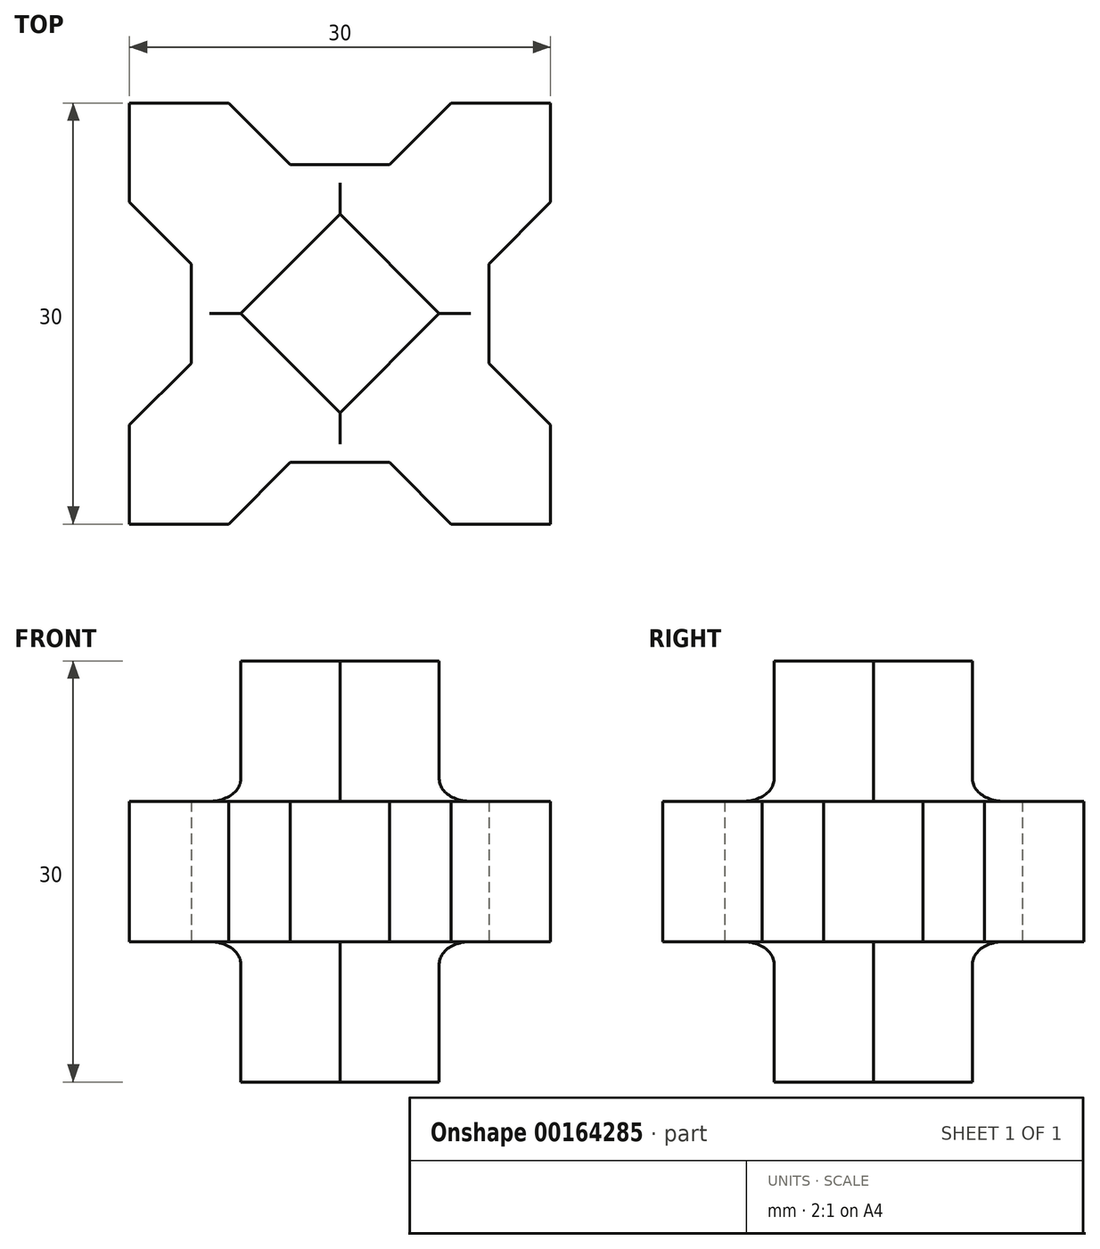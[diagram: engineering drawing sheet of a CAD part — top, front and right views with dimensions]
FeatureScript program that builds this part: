
annotation { "Feature Type Name" : "Feature", "Feature Type Description" : "" }
export const myFeature = defineFeature(function(context is Context, id is Id, definition is map)
    precondition{}
    {
        {
            assignVariable(context, id + "F0", {"name" : "D", "anyValue" : 30 * mm});
        }
        {
            var Q0;
            Q0=qCreatedBy(makeId("Top.planeOp"),FACE);
            var sketch = newSketch(context, id + "F1", { "sketchPlane" : qUnion([Q0])});
            skPoint(sketch, "E0.middle", {"position": v(0, 0) * mm});
            skLineSegment(sketch, "E1", {"start": v(-15, -15) * mm, "end": v(-7.93, -15) * mm});
            skLineSegment(sketch, "E2", {"start": v(-7.93, -15) * mm, "end": v(-3.54, -10.6) * mm});
            skLineSegment(sketch, "E3", {"start": v(-3.54, -10.6) * mm, "end": v(0, -10.6) * mm});
            skLineSegment(sketch, "E4", {"start": v(0, -7.07) * mm, "end": v(-3.54, -3.54) * mm});
            skLineSegment(sketch, "E5", {"start": v(-15, -15) * mm, "end": v(0, 0) * mm, "construction": true});
            skLineSegment(sketch, "E6.MirrorCS", {"start": v(-7.07, 0) * mm, "end": v(-3.54, -3.54) * mm});
            skLineSegment(sketch, "E7.MirrorCS", {"start": v(-10.6, -3.54) * mm, "end": v(-10.6, 0) * mm});
            skLineSegment(sketch, "E8.MirrorCS", {"start": v(-15, -15) * mm, "end": v(-15, -7.93) * mm});
            skLineSegment(sketch, "E9.MirrorCS", {"start": v(-15, -7.93) * mm, "end": v(-10.6, -3.54) * mm});
            skLineSegment(sketch, "E10.1.0", {"start": v(15, -7.93) * mm, "end": v(10.6, -3.54) * mm});
            skLineSegment(sketch, "E10.1.1", {"start": v(0, -7.07) * mm, "end": v(3.54, -3.54) * mm});
            skLineSegment(sketch, "E10.1.2", {"start": v(7.07, 0) * mm, "end": v(3.54, -3.54) * mm});
            skLineSegment(sketch, "E10.1.3", {"start": v(15, -15) * mm, "end": v(7.93, -15) * mm});
            skLineSegment(sketch, "E10.1.4", {"start": v(10.6, -3.54) * mm, "end": v(10.6, 0) * mm});
            skLineSegment(sketch, "E10.1.5", {"start": v(15, -15) * mm, "end": v(15, -7.93) * mm});
            skLineSegment(sketch, "E10.1.6", {"start": v(7.93, -15) * mm, "end": v(3.54, -10.6) * mm});
            skLineSegment(sketch, "E10.1.7", {"start": v(3.54, -10.6) * mm, "end": v(0, -10.6) * mm});
            skLineSegment(sketch, "E10.2.0", {"start": v(7.93, 15) * mm, "end": v(3.54, 10.6) * mm});
            skLineSegment(sketch, "E10.2.1", {"start": v(7.07, 0) * mm, "end": v(3.54, 3.54) * mm});
            skLineSegment(sketch, "E10.2.2", {"start": v(0, 7.07) * mm, "end": v(3.54, 3.54) * mm});
            skLineSegment(sketch, "E10.2.3", {"start": v(15, 15) * mm, "end": v(15, 7.93) * mm});
            skLineSegment(sketch, "E10.2.4", {"start": v(3.54, 10.6) * mm, "end": v(0, 10.6) * mm});
            skLineSegment(sketch, "E10.2.5", {"start": v(15, 15) * mm, "end": v(7.93, 15) * mm});
            skLineSegment(sketch, "E10.2.6", {"start": v(15, 7.93) * mm, "end": v(10.6, 3.54) * mm});
            skLineSegment(sketch, "E10.2.7", {"start": v(10.6, 3.54) * mm, "end": v(10.6, 0) * mm});
            skLineSegment(sketch, "E10.3.0", {"start": v(-15, 7.93) * mm, "end": v(-10.6, 3.54) * mm});
            skLineSegment(sketch, "E10.3.1", {"start": v(0, 7.07) * mm, "end": v(-3.54, 3.54) * mm});
            skLineSegment(sketch, "E10.3.2", {"start": v(-7.07, 0) * mm, "end": v(-3.54, 3.54) * mm});
            skLineSegment(sketch, "E10.3.3", {"start": v(-15, 15) * mm, "end": v(-7.93, 15) * mm});
            skLineSegment(sketch, "E10.3.4", {"start": v(-10.6, 3.54) * mm, "end": v(-10.6, 0) * mm});
            skLineSegment(sketch, "E10.3.5", {"start": v(-15, 15) * mm, "end": v(-15, 7.93) * mm});
            skLineSegment(sketch, "E10.3.6", {"start": v(-7.93, 15) * mm, "end": v(-3.54, 10.6) * mm});
            skLineSegment(sketch, "E10.3.7", {"start": v(-3.54, 10.6) * mm, "end": v(0, 10.6) * mm});
            skSolve(sketch);
        }
        {
            var Q0;
            Q0=makeQuery(id+"F1.imprint","IMPRINT",FACE,{"disambiguationData":[TD([[makeQuery(id+"F1.imprint","IMPRINT",EDGE,{"derivedFrom":sQuery(id+"F1.wireOp",EDGE,"E1")}),1.0]])]});
            var Q1;
            Q1=makeQuery(id+"F1.imprint","IMPRINT",FACE,{"disambiguationData":[TD([[makeQuery(id+"F1.imprint","IMPRINT",EDGE,{"derivedFrom":sQuery(id+"F1.wireOp",EDGE,"E4")}),-1.0]])]});
            extrude(context, id + "F2", {"entities" : qUnion([Q0, Q1]), "depth" : getVariable(context, 'D') / 3, "symmetric" : true});
        }
        {
            var Q0;
            Q0=makeQuery(id+"F1.imprint","IMPRINT",FACE,{"disambiguationData":[TD([[makeQuery(id+"F1.imprint","IMPRINT",EDGE,{"derivedFrom":sQuery(id+"F1.wireOp",EDGE,"E4")}),-1.0]])]});
            extrude(context, id + "F3", {"entities" : qUnion([Q0]), "operationType" : NewBodyOperationType.ADD, "depth" : getVariable(context, 'D'), "symmetric" : true});
        }
        {
            var Q0;
            Q0=makeQuery(id+"F3.boolean.opBoolean","INTERSECT",EDGE,{"derivedFrom":[makeQuery(id+"F2.opExtrude","CAP_FACE",FACE,{"disambiguationData":[OSD([sQuery(id+"F1.wireOp",EDGE,"E1"),sQuery(id+"F1.wireOp",EDGE,"E2"),sQuery(id+"F1.wireOp",EDGE,"E3"),sQuery(id+"F1.wireOp",EDGE,"E7.MirrorCS"),sQuery(id+"F1.wireOp",EDGE,"E8.MirrorCS"),sQuery(id+"F1.wireOp",EDGE,"E9.MirrorCS"),sQuery(id+"F1.wireOp",EDGE,"E10.1.0"),sQuery(id+"F1.wireOp",EDGE,"E10.1.3"),sQuery(id+"F1.wireOp",EDGE,"E10.1.4"),sQuery(id+"F1.wireOp",EDGE,"E10.1.5"),sQuery(id+"F1.wireOp",EDGE,"E10.1.6"),sQuery(id+"F1.wireOp",EDGE,"E10.1.7"),sQuery(id+"F1.wireOp",EDGE,"E10.2.0"),sQuery(id+"F1.wireOp",EDGE,"E10.2.3"),sQuery(id+"F1.wireOp",EDGE,"E10.2.4"),sQuery(id+"F1.wireOp",EDGE,"E10.2.5"),sQuery(id+"F1.wireOp",EDGE,"E10.2.6"),sQuery(id+"F1.wireOp",EDGE,"E10.2.7"),sQuery(id+"F1.wireOp",EDGE,"E10.3.0"),sQuery(id+"F1.wireOp",EDGE,"E10.3.3"),sQuery(id+"F1.wireOp",EDGE,"E10.3.4"),sQuery(id+"F1.wireOp",EDGE,"E10.3.5"),sQuery(id+"F1.wireOp",EDGE,"E10.3.6"),sQuery(id+"F1.wireOp",EDGE,"E10.3.7")])],"isStart":false}),makeQuery(id+"F3.opExtrude","SWEPT_FACE",FACE,{"disambiguationData":[OSD([sQuery(id+"F1.wireOp",EDGE,"E4"),sQuery(id+"F1.wireOp",EDGE,"E6.MirrorCS")])]})]});
            var Q1;
            Q1=makeQuery(id+"F3.boolean.opBoolean","INTERSECT",EDGE,{"derivedFrom":[makeQuery(id+"F2.opExtrude","CAP_FACE",FACE,{"disambiguationData":[OSD([sQuery(id+"F1.wireOp",EDGE,"E1"),sQuery(id+"F1.wireOp",EDGE,"E2"),sQuery(id+"F1.wireOp",EDGE,"E3"),sQuery(id+"F1.wireOp",EDGE,"E7.MirrorCS"),sQuery(id+"F1.wireOp",EDGE,"E8.MirrorCS"),sQuery(id+"F1.wireOp",EDGE,"E9.MirrorCS"),sQuery(id+"F1.wireOp",EDGE,"E10.1.0"),sQuery(id+"F1.wireOp",EDGE,"E10.1.3"),sQuery(id+"F1.wireOp",EDGE,"E10.1.4"),sQuery(id+"F1.wireOp",EDGE,"E10.1.5"),sQuery(id+"F1.wireOp",EDGE,"E10.1.6"),sQuery(id+"F1.wireOp",EDGE,"E10.1.7"),sQuery(id+"F1.wireOp",EDGE,"E10.2.0"),sQuery(id+"F1.wireOp",EDGE,"E10.2.3"),sQuery(id+"F1.wireOp",EDGE,"E10.2.4"),sQuery(id+"F1.wireOp",EDGE,"E10.2.5"),sQuery(id+"F1.wireOp",EDGE,"E10.2.6"),sQuery(id+"F1.wireOp",EDGE,"E10.2.7"),sQuery(id+"F1.wireOp",EDGE,"E10.3.0"),sQuery(id+"F1.wireOp",EDGE,"E10.3.3"),sQuery(id+"F1.wireOp",EDGE,"E10.3.4"),sQuery(id+"F1.wireOp",EDGE,"E10.3.5"),sQuery(id+"F1.wireOp",EDGE,"E10.3.6"),sQuery(id+"F1.wireOp",EDGE,"E10.3.7")])],"isStart":false}),makeQuery(id+"F3.opExtrude","SWEPT_FACE",FACE,{"disambiguationData":[OSD([sQuery(id+"F1.wireOp",EDGE,"E10.1.1"),sQuery(id+"F1.wireOp",EDGE,"E10.1.2")])]})]});
            var Q2;
            Q2=makeQuery(id+"F3.boolean.opBoolean","INTERSECT",EDGE,{"derivedFrom":[makeQuery(id+"F2.opExtrude","CAP_FACE",FACE,{"disambiguationData":[OSD([sQuery(id+"F1.wireOp",EDGE,"E1"),sQuery(id+"F1.wireOp",EDGE,"E2"),sQuery(id+"F1.wireOp",EDGE,"E3"),sQuery(id+"F1.wireOp",EDGE,"E7.MirrorCS"),sQuery(id+"F1.wireOp",EDGE,"E8.MirrorCS"),sQuery(id+"F1.wireOp",EDGE,"E9.MirrorCS"),sQuery(id+"F1.wireOp",EDGE,"E10.1.0"),sQuery(id+"F1.wireOp",EDGE,"E10.1.3"),sQuery(id+"F1.wireOp",EDGE,"E10.1.4"),sQuery(id+"F1.wireOp",EDGE,"E10.1.5"),sQuery(id+"F1.wireOp",EDGE,"E10.1.6"),sQuery(id+"F1.wireOp",EDGE,"E10.1.7"),sQuery(id+"F1.wireOp",EDGE,"E10.2.0"),sQuery(id+"F1.wireOp",EDGE,"E10.2.3"),sQuery(id+"F1.wireOp",EDGE,"E10.2.4"),sQuery(id+"F1.wireOp",EDGE,"E10.2.5"),sQuery(id+"F1.wireOp",EDGE,"E10.2.6"),sQuery(id+"F1.wireOp",EDGE,"E10.2.7"),sQuery(id+"F1.wireOp",EDGE,"E10.3.0"),sQuery(id+"F1.wireOp",EDGE,"E10.3.3"),sQuery(id+"F1.wireOp",EDGE,"E10.3.4"),sQuery(id+"F1.wireOp",EDGE,"E10.3.5"),sQuery(id+"F1.wireOp",EDGE,"E10.3.6"),sQuery(id+"F1.wireOp",EDGE,"E10.3.7")])],"isStart":false}),makeQuery(id+"F3.opExtrude","SWEPT_FACE",FACE,{"disambiguationData":[OSD([sQuery(id+"F1.wireOp",EDGE,"E10.2.1"),sQuery(id+"F1.wireOp",EDGE,"E10.2.2")])]})]});
            var Q3;
            Q3=makeQuery(id+"F3.boolean.opBoolean","INTERSECT",EDGE,{"derivedFrom":[makeQuery(id+"F2.opExtrude","CAP_FACE",FACE,{"disambiguationData":[OSD([sQuery(id+"F1.wireOp",EDGE,"E1"),sQuery(id+"F1.wireOp",EDGE,"E2"),sQuery(id+"F1.wireOp",EDGE,"E3"),sQuery(id+"F1.wireOp",EDGE,"E7.MirrorCS"),sQuery(id+"F1.wireOp",EDGE,"E8.MirrorCS"),sQuery(id+"F1.wireOp",EDGE,"E9.MirrorCS"),sQuery(id+"F1.wireOp",EDGE,"E10.1.0"),sQuery(id+"F1.wireOp",EDGE,"E10.1.3"),sQuery(id+"F1.wireOp",EDGE,"E10.1.4"),sQuery(id+"F1.wireOp",EDGE,"E10.1.5"),sQuery(id+"F1.wireOp",EDGE,"E10.1.6"),sQuery(id+"F1.wireOp",EDGE,"E10.1.7"),sQuery(id+"F1.wireOp",EDGE,"E10.2.0"),sQuery(id+"F1.wireOp",EDGE,"E10.2.3"),sQuery(id+"F1.wireOp",EDGE,"E10.2.4"),sQuery(id+"F1.wireOp",EDGE,"E10.2.5"),sQuery(id+"F1.wireOp",EDGE,"E10.2.6"),sQuery(id+"F1.wireOp",EDGE,"E10.2.7"),sQuery(id+"F1.wireOp",EDGE,"E10.3.0"),sQuery(id+"F1.wireOp",EDGE,"E10.3.3"),sQuery(id+"F1.wireOp",EDGE,"E10.3.4"),sQuery(id+"F1.wireOp",EDGE,"E10.3.5"),sQuery(id+"F1.wireOp",EDGE,"E10.3.6"),sQuery(id+"F1.wireOp",EDGE,"E10.3.7")])],"isStart":false}),makeQuery(id+"F3.opExtrude","SWEPT_FACE",FACE,{"disambiguationData":[OSD([sQuery(id+"F1.wireOp",EDGE,"E10.3.1"),sQuery(id+"F1.wireOp",EDGE,"E10.3.2")])]})]});
            var Q4;
            Q4=makeQuery(id+"F3.boolean.opBoolean","INTERSECT",EDGE,{"derivedFrom":[makeQuery(id+"F2.opExtrude","CAP_FACE",FACE,{"disambiguationData":[OSD([sQuery(id+"F1.wireOp",EDGE,"E1"),sQuery(id+"F1.wireOp",EDGE,"E2"),sQuery(id+"F1.wireOp",EDGE,"E3"),sQuery(id+"F1.wireOp",EDGE,"E7.MirrorCS"),sQuery(id+"F1.wireOp",EDGE,"E8.MirrorCS"),sQuery(id+"F1.wireOp",EDGE,"E9.MirrorCS"),sQuery(id+"F1.wireOp",EDGE,"E10.1.0"),sQuery(id+"F1.wireOp",EDGE,"E10.1.3"),sQuery(id+"F1.wireOp",EDGE,"E10.1.4"),sQuery(id+"F1.wireOp",EDGE,"E10.1.5"),sQuery(id+"F1.wireOp",EDGE,"E10.1.6"),sQuery(id+"F1.wireOp",EDGE,"E10.1.7"),sQuery(id+"F1.wireOp",EDGE,"E10.2.0"),sQuery(id+"F1.wireOp",EDGE,"E10.2.3"),sQuery(id+"F1.wireOp",EDGE,"E10.2.4"),sQuery(id+"F1.wireOp",EDGE,"E10.2.5"),sQuery(id+"F1.wireOp",EDGE,"E10.2.6"),sQuery(id+"F1.wireOp",EDGE,"E10.2.7"),sQuery(id+"F1.wireOp",EDGE,"E10.3.0"),sQuery(id+"F1.wireOp",EDGE,"E10.3.3"),sQuery(id+"F1.wireOp",EDGE,"E10.3.4"),sQuery(id+"F1.wireOp",EDGE,"E10.3.5"),sQuery(id+"F1.wireOp",EDGE,"E10.3.6"),sQuery(id+"F1.wireOp",EDGE,"E10.3.7")])],"isStart":true}),makeQuery(id+"F3.opExtrude","SWEPT_FACE",FACE,{"disambiguationData":[OSD([sQuery(id+"F1.wireOp",EDGE,"E10.3.1"),sQuery(id+"F1.wireOp",EDGE,"E10.3.2")])]})]});
            var Q5;
            Q5=makeQuery(id+"F3.boolean.opBoolean","INTERSECT",EDGE,{"derivedFrom":[makeQuery(id+"F2.opExtrude","CAP_FACE",FACE,{"disambiguationData":[OSD([sQuery(id+"F1.wireOp",EDGE,"E1"),sQuery(id+"F1.wireOp",EDGE,"E2"),sQuery(id+"F1.wireOp",EDGE,"E3"),sQuery(id+"F1.wireOp",EDGE,"E7.MirrorCS"),sQuery(id+"F1.wireOp",EDGE,"E8.MirrorCS"),sQuery(id+"F1.wireOp",EDGE,"E9.MirrorCS"),sQuery(id+"F1.wireOp",EDGE,"E10.1.0"),sQuery(id+"F1.wireOp",EDGE,"E10.1.3"),sQuery(id+"F1.wireOp",EDGE,"E10.1.4"),sQuery(id+"F1.wireOp",EDGE,"E10.1.5"),sQuery(id+"F1.wireOp",EDGE,"E10.1.6"),sQuery(id+"F1.wireOp",EDGE,"E10.1.7"),sQuery(id+"F1.wireOp",EDGE,"E10.2.0"),sQuery(id+"F1.wireOp",EDGE,"E10.2.3"),sQuery(id+"F1.wireOp",EDGE,"E10.2.4"),sQuery(id+"F1.wireOp",EDGE,"E10.2.5"),sQuery(id+"F1.wireOp",EDGE,"E10.2.6"),sQuery(id+"F1.wireOp",EDGE,"E10.2.7"),sQuery(id+"F1.wireOp",EDGE,"E10.3.0"),sQuery(id+"F1.wireOp",EDGE,"E10.3.3"),sQuery(id+"F1.wireOp",EDGE,"E10.3.4"),sQuery(id+"F1.wireOp",EDGE,"E10.3.5"),sQuery(id+"F1.wireOp",EDGE,"E10.3.6"),sQuery(id+"F1.wireOp",EDGE,"E10.3.7")])],"isStart":true}),makeQuery(id+"F3.opExtrude","SWEPT_FACE",FACE,{"disambiguationData":[OSD([sQuery(id+"F1.wireOp",EDGE,"E4"),sQuery(id+"F1.wireOp",EDGE,"E6.MirrorCS")])]})]});
            var Q6;
            Q6=makeQuery(id+"F3.boolean.opBoolean","INTERSECT",EDGE,{"derivedFrom":[makeQuery(id+"F2.opExtrude","CAP_FACE",FACE,{"disambiguationData":[OSD([sQuery(id+"F1.wireOp",EDGE,"E1"),sQuery(id+"F1.wireOp",EDGE,"E2"),sQuery(id+"F1.wireOp",EDGE,"E3"),sQuery(id+"F1.wireOp",EDGE,"E7.MirrorCS"),sQuery(id+"F1.wireOp",EDGE,"E8.MirrorCS"),sQuery(id+"F1.wireOp",EDGE,"E9.MirrorCS"),sQuery(id+"F1.wireOp",EDGE,"E10.1.0"),sQuery(id+"F1.wireOp",EDGE,"E10.1.3"),sQuery(id+"F1.wireOp",EDGE,"E10.1.4"),sQuery(id+"F1.wireOp",EDGE,"E10.1.5"),sQuery(id+"F1.wireOp",EDGE,"E10.1.6"),sQuery(id+"F1.wireOp",EDGE,"E10.1.7"),sQuery(id+"F1.wireOp",EDGE,"E10.2.0"),sQuery(id+"F1.wireOp",EDGE,"E10.2.3"),sQuery(id+"F1.wireOp",EDGE,"E10.2.4"),sQuery(id+"F1.wireOp",EDGE,"E10.2.5"),sQuery(id+"F1.wireOp",EDGE,"E10.2.6"),sQuery(id+"F1.wireOp",EDGE,"E10.2.7"),sQuery(id+"F1.wireOp",EDGE,"E10.3.0"),sQuery(id+"F1.wireOp",EDGE,"E10.3.3"),sQuery(id+"F1.wireOp",EDGE,"E10.3.4"),sQuery(id+"F1.wireOp",EDGE,"E10.3.5"),sQuery(id+"F1.wireOp",EDGE,"E10.3.6"),sQuery(id+"F1.wireOp",EDGE,"E10.3.7")])],"isStart":true}),makeQuery(id+"F3.opExtrude","SWEPT_FACE",FACE,{"disambiguationData":[OSD([sQuery(id+"F1.wireOp",EDGE,"E10.1.1"),sQuery(id+"F1.wireOp",EDGE,"E10.1.2")])]})]});
            var Q7;
            Q7=makeQuery(id+"F3.boolean.opBoolean","INTERSECT",EDGE,{"derivedFrom":[makeQuery(id+"F2.opExtrude","CAP_FACE",FACE,{"disambiguationData":[OSD([sQuery(id+"F1.wireOp",EDGE,"E1"),sQuery(id+"F1.wireOp",EDGE,"E2"),sQuery(id+"F1.wireOp",EDGE,"E3"),sQuery(id+"F1.wireOp",EDGE,"E7.MirrorCS"),sQuery(id+"F1.wireOp",EDGE,"E8.MirrorCS"),sQuery(id+"F1.wireOp",EDGE,"E9.MirrorCS"),sQuery(id+"F1.wireOp",EDGE,"E10.1.0"),sQuery(id+"F1.wireOp",EDGE,"E10.1.3"),sQuery(id+"F1.wireOp",EDGE,"E10.1.4"),sQuery(id+"F1.wireOp",EDGE,"E10.1.5"),sQuery(id+"F1.wireOp",EDGE,"E10.1.6"),sQuery(id+"F1.wireOp",EDGE,"E10.1.7"),sQuery(id+"F1.wireOp",EDGE,"E10.2.0"),sQuery(id+"F1.wireOp",EDGE,"E10.2.3"),sQuery(id+"F1.wireOp",EDGE,"E10.2.4"),sQuery(id+"F1.wireOp",EDGE,"E10.2.5"),sQuery(id+"F1.wireOp",EDGE,"E10.2.6"),sQuery(id+"F1.wireOp",EDGE,"E10.2.7"),sQuery(id+"F1.wireOp",EDGE,"E10.3.0"),sQuery(id+"F1.wireOp",EDGE,"E10.3.3"),sQuery(id+"F1.wireOp",EDGE,"E10.3.4"),sQuery(id+"F1.wireOp",EDGE,"E10.3.5"),sQuery(id+"F1.wireOp",EDGE,"E10.3.6"),sQuery(id+"F1.wireOp",EDGE,"E10.3.7")])],"isStart":true}),makeQuery(id+"F3.opExtrude","SWEPT_FACE",FACE,{"disambiguationData":[OSD([sQuery(id+"F1.wireOp",EDGE,"E10.2.1"),sQuery(id+"F1.wireOp",EDGE,"E10.2.2")])]})]});
            fillet(context, id + "F4", {"entities" : qUnion([Q0, Q1, Q2, Q3, Q4, Q5, Q6, Q7]), "radius" : getVariable(context, 'D') / 19, "tangentPropagation" : true, "allowEdgeOverflow" : false});
        }
    });
